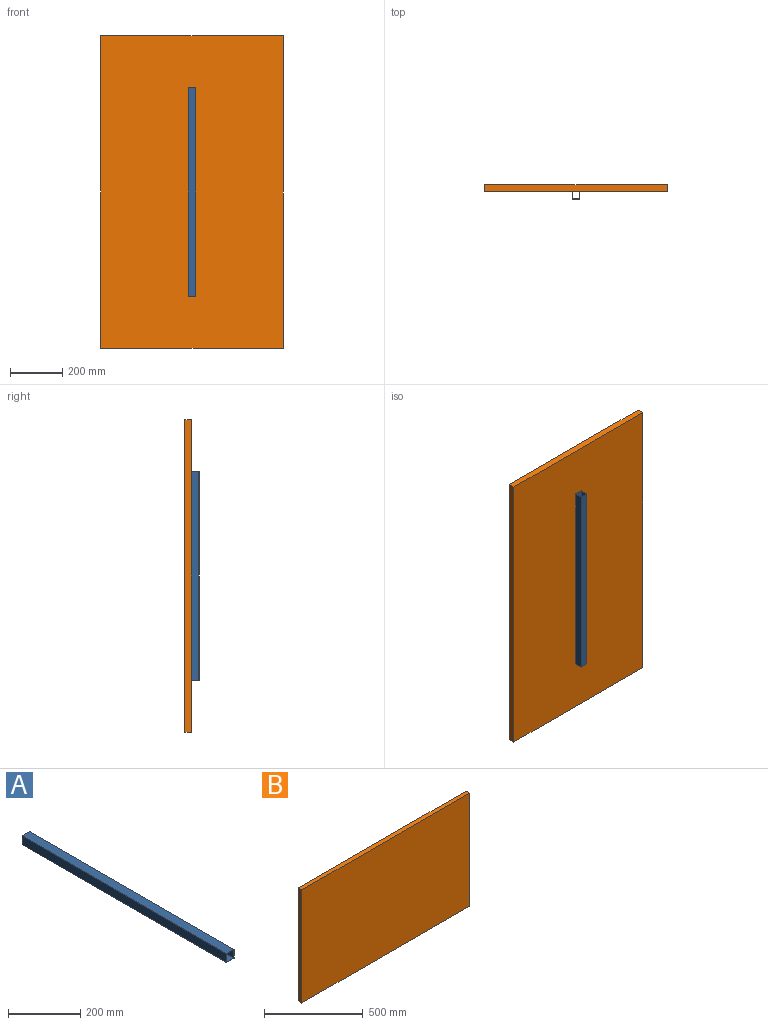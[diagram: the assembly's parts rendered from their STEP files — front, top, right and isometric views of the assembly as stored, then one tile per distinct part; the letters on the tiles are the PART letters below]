
ASSEMBLY  parts=2 mates=3
PART A: 10 faces, bbox 30x800x30 mm
  f0: plane 800x28mm, normal (0,0,-1), area 22400mm2, adj f1,f7,f8,f9
  f1: plane 800x28mm, normal (-1,0,0), area 22400mm2, adj f0,f2,f8,f9
  f2: plane 800x28mm, normal (0,0,1), area 22400mm2, adj f1,f7,f8,f9
  f3: plane 800x30mm, normal (1,0,0), area 24000mm2, adj f4,f6,f8,f9
  f4: plane 800x30mm, normal (0,0,1), area 24000mm2, adj f3,f5,f8,f9
  f5: plane 800x30mm, normal (-1,0,0), area 24000mm2, adj f4,f6,f8,f9
  f6: plane 800x30mm, normal (0,0,-1), area 24000mm2, adj f3,f5,f8,f9
  f7: plane 800x28mm, normal (1,0,0), area 22400mm2, adj f0,f2,f8,f9
  f8: plane 30x30mm, normal (0,-1,0), area 116mm2, adj f0,f1,f2,f3,f4,f5,f6,f7
  f9: plane 30x30mm, normal (0,1,0), area 116mm2, adj f0,f1,f2,f3,f4,f5,f6,f7
PART B: 6 faces, bbox 1200x25x700 mm
  f0: plane 700x25mm, normal (1,0,0), area 17500mm2, adj f1,f3,f4,f5
  f1: plane 1200x25mm, normal (0,0,1), area 30000mm2, adj f0,f2,f4,f5
  f2: plane 700x25mm, normal (-1,0,0), area 17500mm2, adj f1,f3,f4,f5
  f3: plane 1200x25mm, normal (0,0,-1), area 30000mm2, adj f0,f2,f4,f5
  f4: plane 1200x700mm, normal (0,-1,0), area 840000mm2, adj f0,f1,f2,f3
  f5: plane 1200x700mm, normal (0,1,0), area 840000mm2, adj f0,f1,f2,f3
PLACE A rot(axis=(-1,0,0),90deg) t=(-374.75,102.36,-110.05)mm
PLACE B rot(axis=(-0.71,0,0.71),180deg) t=(-374.75,117.36,289.95)mm
MATE fastened A.f4 <-> B.f5  axis (0,1,0) through (-374.75,117.36,289.95)mm
MATE parallel B.f4 <-> A.f4  axis (0,1,0) through (-374.75,142.36,289.95)mm
MATE parallel B.f3 <-> A.f5  axis (1,0,0) through (-24.75,129.86,289.95)mm
